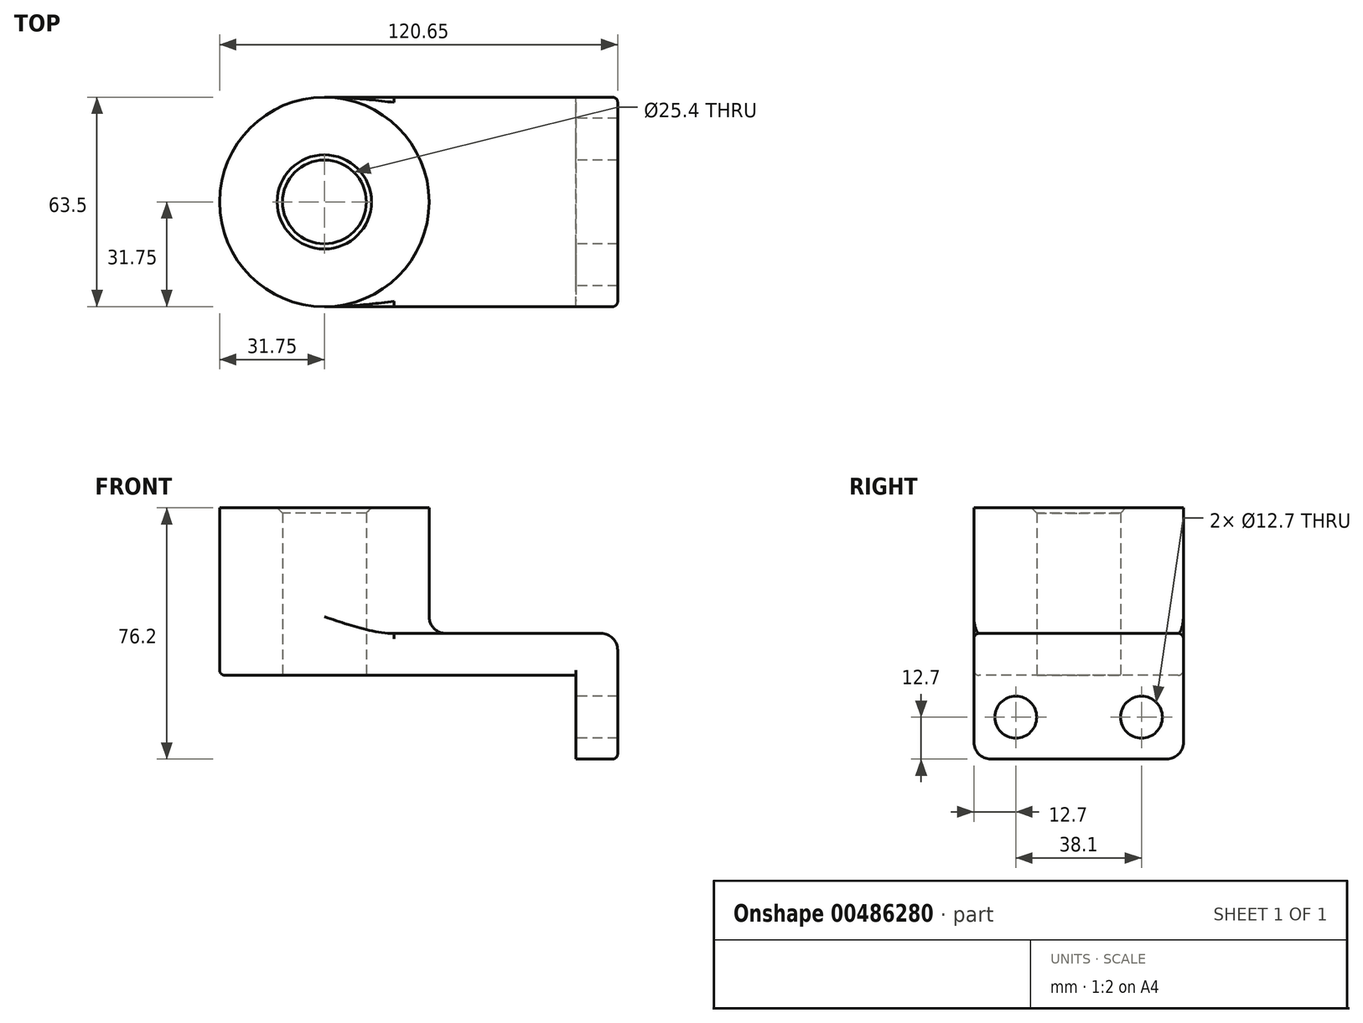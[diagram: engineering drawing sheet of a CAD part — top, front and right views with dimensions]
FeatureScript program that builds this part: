
annotation { "Feature Type Name" : "Feature", "Feature Type Description" : "" }
export const myFeature = defineFeature(function(context is Context, id is Id, definition is map)
    precondition{}
    {
        {
            var Q0;
            Q0=qCreatedBy(makeId("Top.planeOp"),FACE);
            var sketch = newSketch(context, id + "F0", { "sketchPlane" : qUnion([Q0])});
            skLineSegment(sketch, "E0.bottom", {"start": v(38.1, 31.75) * mm, "end": v(-38.1, 31.75) * mm});
            skLineSegment(sketch, "E0.top", {"start": v(38.1, -31.75) * mm, "end": v(-38.1, -31.75) * mm});
            skLineSegment(sketch, "E0.left", {"start": v(38.1, 31.75) * mm, "end": v(38.1, -31.75) * mm});
            skLineSegment(sketch, "E0.right", {"start": v(-38.1, 31.75) * mm, "end": v(-38.1, -31.75) * mm});
            skPoint(sketch, "E0.middle", {"position": v(0, 0) * mm});
            skCircle(sketch, "E1", {"center": v(-38.1, 0) * mm, "radius": 31.75 * mm});
            skCircle(sketch, "E2", {"center": v(-38.1, 0) * mm, "radius": 12.7 * mm});
            skSolve(sketch);
        }
        {
            var Q0;
            Q0 = qSketchRegion(id + "F0", true);
            extrude(context, id + "F1", {"entities" : qUnion([Q0]), "depth" : 12.7 * mm});
        }
        {
            var Q0;
            {var subQ1=sQuery(id+"F0.wireOp",EDGE,"E0.right");var subQ3=sQuery(id+"F0.wireOp",EDGE,"E2");var subQ4=makeQuery(id+"F0.imprint","INTERSECT",VERTEX,{"disambiguationData":[OD(0.0)],"derivedFrom":[subQ1,subQ3]});Q0=makeQuery(id+"F0.imprint","IMPRINT",FACE,{"disambiguationData":[TD([[makeQuery(id+"F0.imprint","IMPRINT",EDGE,{"disambiguationData":[TD([[subQ4,-1.0]])],"derivedFrom":subQ3}),-1.0]])]});}
            var Q1;
            {var subQ1=sQuery(id+"F0.wireOp",EDGE,"E0.right");var subQ3=sQuery(id+"F0.wireOp",EDGE,"E2");var subQ4=makeQuery(id+"F0.imprint","INTERSECT",VERTEX,{"disambiguationData":[OD(0.0)],"derivedFrom":[subQ1,subQ3]});Q1=makeQuery(id+"F0.imprint","IMPRINT",FACE,{"disambiguationData":[TD([[makeQuery(id+"F0.imprint","IMPRINT",EDGE,{"disambiguationData":[TD([[subQ4,1.0]])],"derivedFrom":subQ3}),-1.0]])]});}
            extrude(context, id + "F2", {"entities" : qUnion([Q0, Q1]), "operationType" : NewBodyOperationType.ADD, "depth" : 50.8 * mm});
        }
        {
            var Q0;
            Q0=makeQuery(id+"F1.opExtrude","SWEPT_FACE",FACE,{"disambiguationData":[OSD([sQuery(id+"F0.wireOp",EDGE,"E0.left")])]});
            var sketch = newSketch(context, id + "F3", { "sketchPlane" : qUnion([Q0])});
            skLineSegment(sketch, "E3.bottom", {"start": v(-31.75, 12.7) * mm, "end": v(31.75, 12.7) * mm});
            skLineSegment(sketch, "E3.top", {"start": v(-31.75, -25.4) * mm, "end": v(31.75, -25.4) * mm});
            skLineSegment(sketch, "E3.left", {"start": v(-31.75, 12.7) * mm, "end": v(-31.75, -25.4) * mm});
            skLineSegment(sketch, "E3.right", {"start": v(31.75, 12.7) * mm, "end": v(31.75, -25.4) * mm});
            skCircle(sketch, "E4", {"center": v(-19.05, -12.7) * mm, "radius": 6.35 * mm});
            skLineSegment(sketch, "E5", {"start": v(0, 0) * mm, "end": v(0, -25.4) * mm});
            skCircle(sketch, "E6.MirrorC", {"center": v(19.05, -12.7) * mm, "radius": 6.35 * mm});
            skSolve(sketch);
        }
        {
            var Q0;
            {var subQ1=sQuery(id+"F3.wireOp",EDGE,"E5");Q0=makeQuery(id+"F3.imprint","IMPRINT",FACE,{"disambiguationData":[TD([[makeQuery(id+"F3.imprint","IMPRINT",EDGE,{"derivedFrom":subQ1}),1.0]])]});}
            var Q1;
            {var subQ3=sQuery(id+"F3.wireOp",EDGE,"E3.bottom");Q1=makeQuery(id+"F3.imprint","IMPRINT",FACE,{"disambiguationData":[TD([[makeQuery(id+"F3.imprint","IMPRINT",EDGE,{"derivedFrom":subQ3}),1.0]])]});}
            var Q2;
            {var subQ0=sQuery(id+"F3.wireOp",EDGE,"E4");Q2=makeQuery(id+"F3.imprint","IMPRINT",FACE,{"disambiguationData":[TD([[makeQuery(id+"F3.imprint","IMPRINT",EDGE,{"derivedFrom":subQ0}),-1.0]])]});}
            extrude(context, id + "F4", {"entities" : qUnion([Q0, Q1, Q2]), "operationType" : NewBodyOperationType.ADD, "depth" : 12.7 * mm});
        }
        {
            var Q0;
            {var subQ0=sQuery(id+"F0.wireOp",EDGE,"E1");Q0=makeQuery(id+"F2.boolean.opBoolean","INTERSECT",EDGE,{"derivedFrom":[makeQuery(id+"F1.opExtrude","CAP_FACE",FACE,{"disambiguationData":[OSD([sQuery(id+"F0.wireOp",EDGE,"E0.bottom"),sQuery(id+"F0.wireOp",EDGE,"E0.top"),sQuery(id+"F0.wireOp",EDGE,"E0.left"),subQ0,sQuery(id+"F0.wireOp",EDGE,"E2")])],"isStart":false}),makeQuery(id+"F2.opExtrude","SWEPT_FACE",FACE,{"disambiguationData":[OSD([subQ0])]})]});}
            var Q1;
            Q1=makeQuery(id+"F4.opExtrude","CAP_EDGE",EDGE,{"disambiguationData":[OSD([sQuery(id+"F3.wireOp",EDGE,"E3.bottom")])],"isStart":false});
            var Q2;
            Q2=makeQuery(id+"F4.opExtrude","SWEPT_EDGE",EDGE,{"disambiguationData":[OSD([sQuery(id+"F3.wireOp",EDGE,"E3.top"),sQuery(id+"F3.wireOp",EDGE,"E3.right")])]});
            var Q3;
            Q3=makeQuery(id+"F4.opExtrude","SWEPT_EDGE",EDGE,{"disambiguationData":[OSD([sQuery(id+"F3.wireOp",EDGE,"E3.top"),sQuery(id+"F3.wireOp",EDGE,"E3.left")])]});
            fillet(context, id + "F5", {"entities" : qUnion([Q0, Q1, Q2, Q3]), "radius" : 5.08 * mm, "tangentPropagation" : true, "allowEdgeOverflow" : false});
        }
        {
            var Q0;
            Q0=makeQuery(id+"F4.boolean.opBoolean","MERGE",EDGE,{"derivedFrom":[makeQuery(id+"F1.opExtrude","CAP_EDGE",EDGE,{"disambiguationData":[OSD([sQuery(id+"F0.wireOp",EDGE,"E0.top")])],"isStart":false}),makeQuery(id+"F4.opExtrude","SWEPT_EDGE",EDGE,{"disambiguationData":[OSD([sQuery(id+"F3.wireOp",EDGE,"E3.bottom"),sQuery(id+"F3.wireOp",EDGE,"E3.left")])]})]});
            var Q1;
            Q1=makeQuery(id+"F4.boolean.opBoolean","MERGE",EDGE,{"derivedFrom":[makeQuery(id+"F1.opExtrude","CAP_EDGE",EDGE,{"disambiguationData":[OSD([sQuery(id+"F0.wireOp",EDGE,"E0.bottom")])],"isStart":false}),makeQuery(id+"F4.opExtrude","SWEPT_EDGE",EDGE,{"disambiguationData":[OSD([sQuery(id+"F3.wireOp",EDGE,"E3.bottom"),sQuery(id+"F3.wireOp",EDGE,"E3.right")])]})]});
            var Q2;
            {var subQ0=sQuery(id+"F0.wireOp",EDGE,"E0.left");var subQ1=sQuery(id+"F3.wireOp",EDGE,"E6.MirrorC");var subQ2=sQuery(id+"F3.wireOp",EDGE,"E4");Q2=makeQuery(id+"F4.boolean.opBoolean","SPLIT",EDGE,{"disambiguationData":[TD([makeQuery(id+"F1.opExtrude","CAP_FACE",FACE,{"disambiguationData":[OSD([sQuery(id+"F0.wireOp",EDGE,"E0.bottom"),sQuery(id+"F0.wireOp",EDGE,"E0.top"),subQ0,sQuery(id+"F0.wireOp",EDGE,"E1"),sQuery(id+"F0.wireOp",EDGE,"E2")])],"isStart":true}),makeQuery(id+"F4.opExtrude","CAP_FACE",FACE,{"disambiguationData":[OSD([sQuery(id+"F3.wireOp",EDGE,"E3.bottom"),sQuery(id+"F3.wireOp",EDGE,"E3.top"),sQuery(id+"F3.wireOp",EDGE,"E3.left"),sQuery(id+"F3.wireOp",EDGE,"E3.right"),subQ2,subQ1])],"isStart":true}),makeQuery(id+"F4.opExtrude","SWEPT_FACE",FACE,{"disambiguationData":[OSD([subQ2])]}),makeQuery(id+"F4.opExtrude","SWEPT_FACE",FACE,{"disambiguationData":[OSD([subQ1])]})])],"derivedFrom":makeQuery(id+"F1.opExtrude","CAP_EDGE",EDGE,{"disambiguationData":[OSD([subQ0])],"isStart":true})});}
            var Q3;
            Q3=makeQuery(id+"F1.opExtrude","CAP_EDGE",EDGE,{"disambiguationData":[OSD([sQuery(id+"F0.wireOp",EDGE,"E0.top")])],"isStart":true});
            fillet(context, id + "F6", {"entities" : qUnion([Q0, Q1, Q2, Q3]), "radius" : 1.59 * mm, "tangentPropagation" : true, "allowEdgeOverflow" : false});
        }
        {
            var Q0;
            Q0=makeQuery(id+"F2.opExtrude","CAP_EDGE",EDGE,{"disambiguationData":[OSD([sQuery(id+"F0.wireOp",EDGE,"E2")])],"isStart":false});
            chamfer(context, id + "F7", {"entities" : qUnion([Q0]), "width" : 1.59 * mm, "tangentPropagation" : true});
        }
    });
